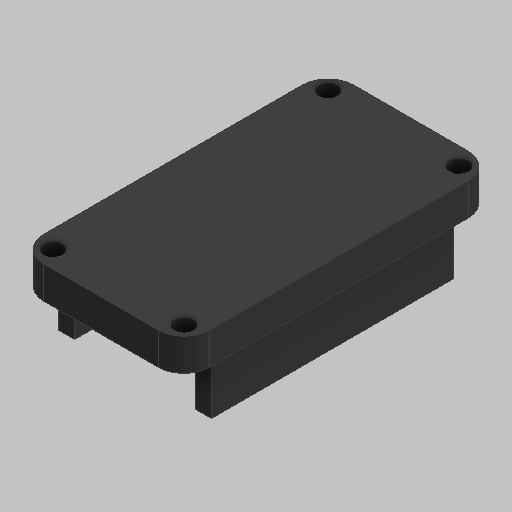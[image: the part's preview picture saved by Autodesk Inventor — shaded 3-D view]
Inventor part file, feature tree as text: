
AUTODESK INVENTOR PART (.ipt)
format: ipt  version: 2025 (Build 290162010, 162A)  size: 158,208 bytes
history: native  units: mm
features: other x4, extrude x3, sketch x3, fillet x2
ambient origin geometry x8: Origin, YZ Plane, XZ Plane, XY Plane, X Axis, Y Axis, Z Axis, Center Point
bodies: Body1 (feature_tree)
feature tree (12):
  other  "Sólido1"
  extrude  "Extrusión1"  Depth=25.7mm
  fillet  "Empalme1"  Radius=12.565mm
  fillet  "Empalme2"  Radius=24.0mm
  extrude  "Extrusión2"  Depth=4.0mm
  extrude  "Extrusión3"  Depth=8.0mm
  sketch  "Boceto1"  dims[d0=48.0mm d1=25.7mm d2=12.565mm d3=24.0mm]
  sketch  "Boceto2"  dims[d4=5.0mm d5=0.0mm d6=4.0mm]
  sketch  "Boceto3"  dims[d7=4.0mm d8=3.0mm d9=2.7mm d10=2.7mm d11=10.0mm d12=0.0mm d13=37.5mm d14=2.5mm d15=1.0mm d16=5.25mm d17=5.25mm d18=1.0mm d19=8.0mm d20=0.0mm d21=2.7mm d22=2.7mm]
  other  "Finish1"
  other  "Finish2"
  other  "Finish3"
